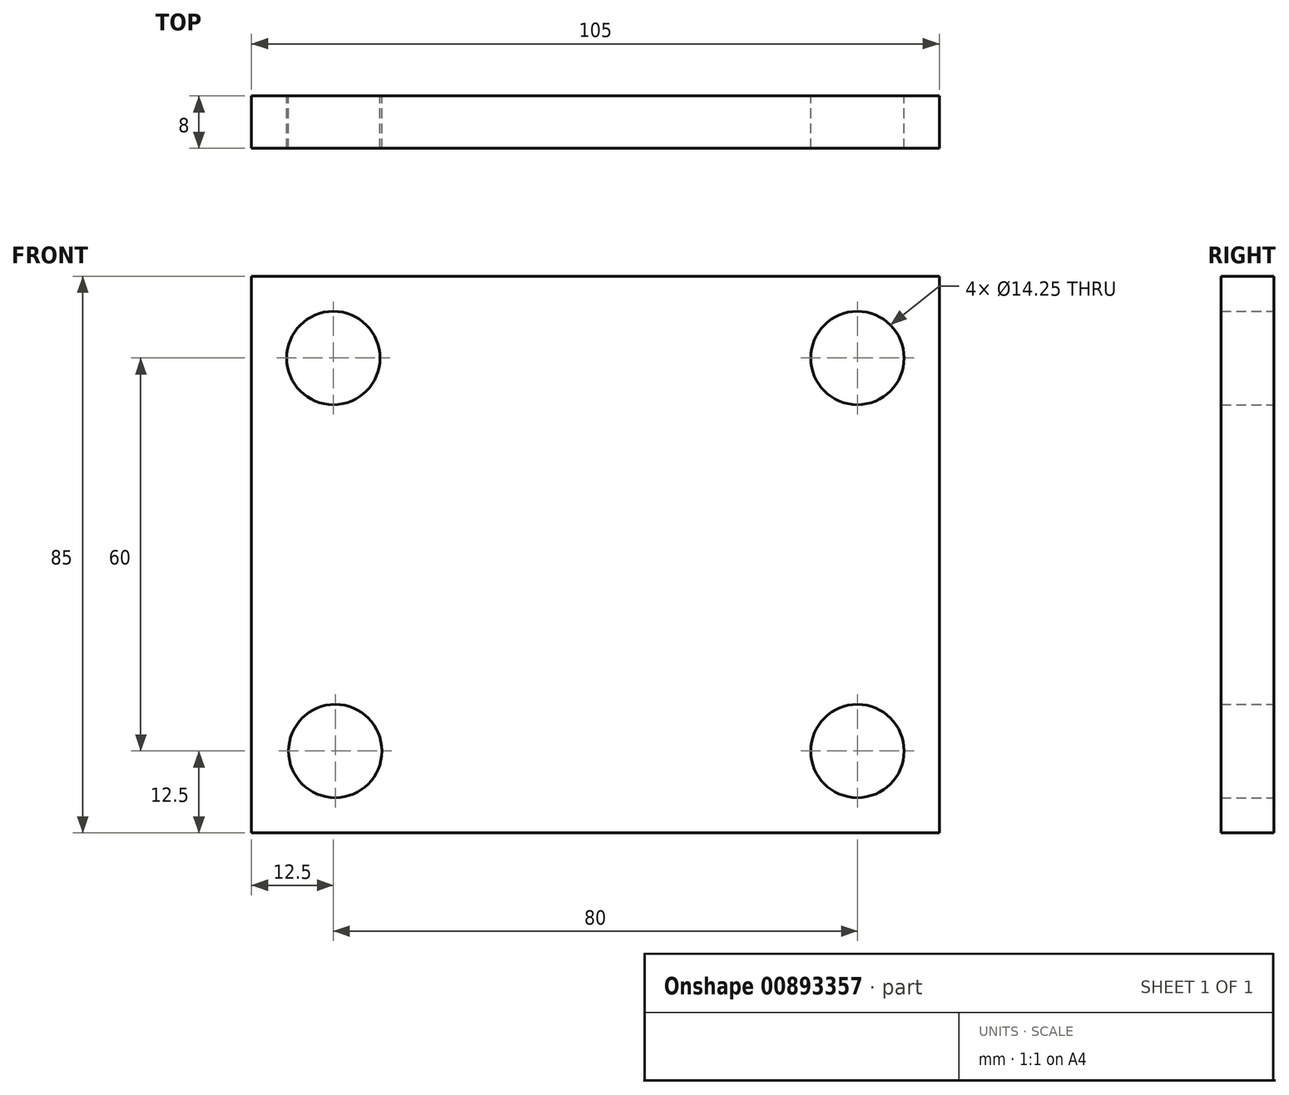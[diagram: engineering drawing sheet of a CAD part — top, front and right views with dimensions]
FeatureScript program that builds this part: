
annotation { "Feature Type Name" : "Feature", "Feature Type Description" : "" }
export const myFeature = defineFeature(function(context is Context, id is Id, definition is map)
    precondition{}
    {
        {
            var Q0;
            Q0=qCreatedBy(makeId("Front.planeOp"),FACE);
            var sketch = newSketch(context, id + "F0", { "sketchPlane" : qUnion([Q0])});
            skLineSegment(sketch, "E0.bottom", {"start": v(52.5, 42.5) * mm, "end": v(-52.5, 42.5) * mm});
            skLineSegment(sketch, "E0.top", {"start": v(52.5, -42.5) * mm, "end": v(-52.5, -42.5) * mm});
            skLineSegment(sketch, "E0.left", {"start": v(52.5, 42.5) * mm, "end": v(52.5, -42.5) * mm});
            skLineSegment(sketch, "E0.right", {"start": v(-52.5, 42.5) * mm, "end": v(-52.5, -42.5) * mm});
            skPoint(sketch, "E0.middle", {"position": v(0, 0) * mm});
            skCircle(sketch, "E1", {"center": v(-40, 30) * mm, "radius": 3.67 * mm});
            skCircle(sketch, "E2", {"center": v(-39.71, -30) * mm, "radius": 3.3 * mm});
            skLineSegment(sketch, "E3", {"start": v(-40, 30) * mm, "end": v(40, 30) * mm});
            skCircle(sketch, "E4", {"center": v(40, 30) * mm, "radius": 3.44 * mm});
            skLineSegment(sketch, "E5", {"start": v(40, 30) * mm, "end": v(40, -30) * mm});
            skCircle(sketch, "E6", {"center": v(40, -30) * mm, "radius": 3.54 * mm});
            skSolve(sketch);
        }
        {
            var Q0;
            Q0=makeQuery(id+"F0.imprint","IMPRINT",FACE,{"disambiguationData":[TD([[makeQuery(id+"F0.imprint","IMPRINT",EDGE,{"derivedFrom":sQuery(id+"F0.wireOp",EDGE,"E0.bottom")}),1.0]])]});
            var Q1;
            Q1=makeQuery(id+"F0.imprint","IMPRINT",FACE,{"disambiguationData":[TD([[makeQuery(id+"F0.imprint","IMPRINT",EDGE,{"derivedFrom":sQuery(id+"F0.wireOp",EDGE,"E1")}),1.0]])]});
            var Q2;
            {var subQ0=sQuery(id+"F0.wireOp",EDGE,"E5");var subQ1=sQuery(id+"F0.wireOp",EDGE,"E3");var subQ2=makeQuery(id+"F0.imprint","INTERSECT",VERTEX,{"derivedFrom":[subQ1,subQ0]});Q2=makeQuery(id+"F0.imprint","IMPRINT",FACE,{"disambiguationData":[TD([[makeQuery(id+"F0.imprint","IMPRINT",EDGE,{"disambiguationData":[TD([[subQ2,1.0]])],"derivedFrom":subQ1}),1.0]])]});}
            var Q3;
            {var subQ0=sQuery(id+"F0.wireOp",EDGE,"E5");var subQ1=sQuery(id+"F0.wireOp",EDGE,"E3");var subQ2=makeQuery(id+"F0.imprint","INTERSECT",VERTEX,{"derivedFrom":[subQ1,subQ0]});Q3=makeQuery(id+"F0.imprint","IMPRINT",FACE,{"disambiguationData":[TD([[makeQuery(id+"F0.imprint","IMPRINT",EDGE,{"disambiguationData":[TD([[subQ2,1.0]])],"derivedFrom":subQ1}),-1.0]])]});}
            var Q4;
            Q4=makeQuery(id+"F0.imprint","IMPRINT",FACE,{"disambiguationData":[TD([[makeQuery(id+"F0.imprint","IMPRINT",EDGE,{"derivedFrom":sQuery(id+"F0.wireOp",EDGE,"E6")}),1.0]])]});
            var Q5;
            Q5=makeQuery(id+"F0.imprint","IMPRINT",FACE,{"disambiguationData":[TD([[makeQuery(id+"F0.imprint","IMPRINT",EDGE,{"derivedFrom":sQuery(id+"F0.wireOp",EDGE,"E2")}),1.0]])]});
            extrude(context, id + "F1", {"entities" : qUnion([Q0, Q1, Q2, Q3, Q4, Q5]), "depth" : 8 * mm, "offsetDistance" : 25 * mm});
        }
        {
            var Q0;
            Q0=sQuery(id+"F0.wireOp",VERTEX,"E3.start");
            var Q1;
            Q1=sQuery(id+"F0.wireOp",VERTEX,"E3.end");
            var Q2;
            Q2=sQuery(id+"F0.wireOp",VERTEX,"E5.end");
            var Q3;
            Q3=sQuery(id+"F0.wireOp",VERTEX,"E2.center");
            var Q4;
            Q4=makeQuery(id+"F1.opExtrude","SWEPT_BODY",BODY,{"disambiguationData":[OSD([sQuery(id+"F0.wireOp",EDGE,"E0.bottom"),sQuery(id+"F0.wireOp",EDGE,"E0.top"),sQuery(id+"F0.wireOp",EDGE,"E0.left"),sQuery(id+"F0.wireOp",EDGE,"E0.right")])]});
            hole(context, id + "F2", {"style" : HoleStyle.C_BORE, "endStyle" : HoleEndStyle.THROUGH, "oppositeDirection" : true, "standardTappedOrClearance" : lookupTablePath({ "fit" : "Standard", "standard" : "ISO", "size" : "M8", "type" : "Clearance" }), "standardBlindInLast" : lookupTablePath({ "fit" : "Standard", "standard" : "ISO", "size" : "M8", "type" : "Clearance" }), "holeDiameter" : 8.8 * mm, "cBoreDiameter" : 14.25 * mm, "cBoreDepth" : 8 * mm, "majorDiameter" : 5 * mm, "isTappedThrough" : true, "tappedDepth" : 12 * mm, "tapClearance" : 3, "locations" : qUnion([Q0, Q1, Q2, Q3]), "scope" : qUnion([Q4])});
        }
    });
